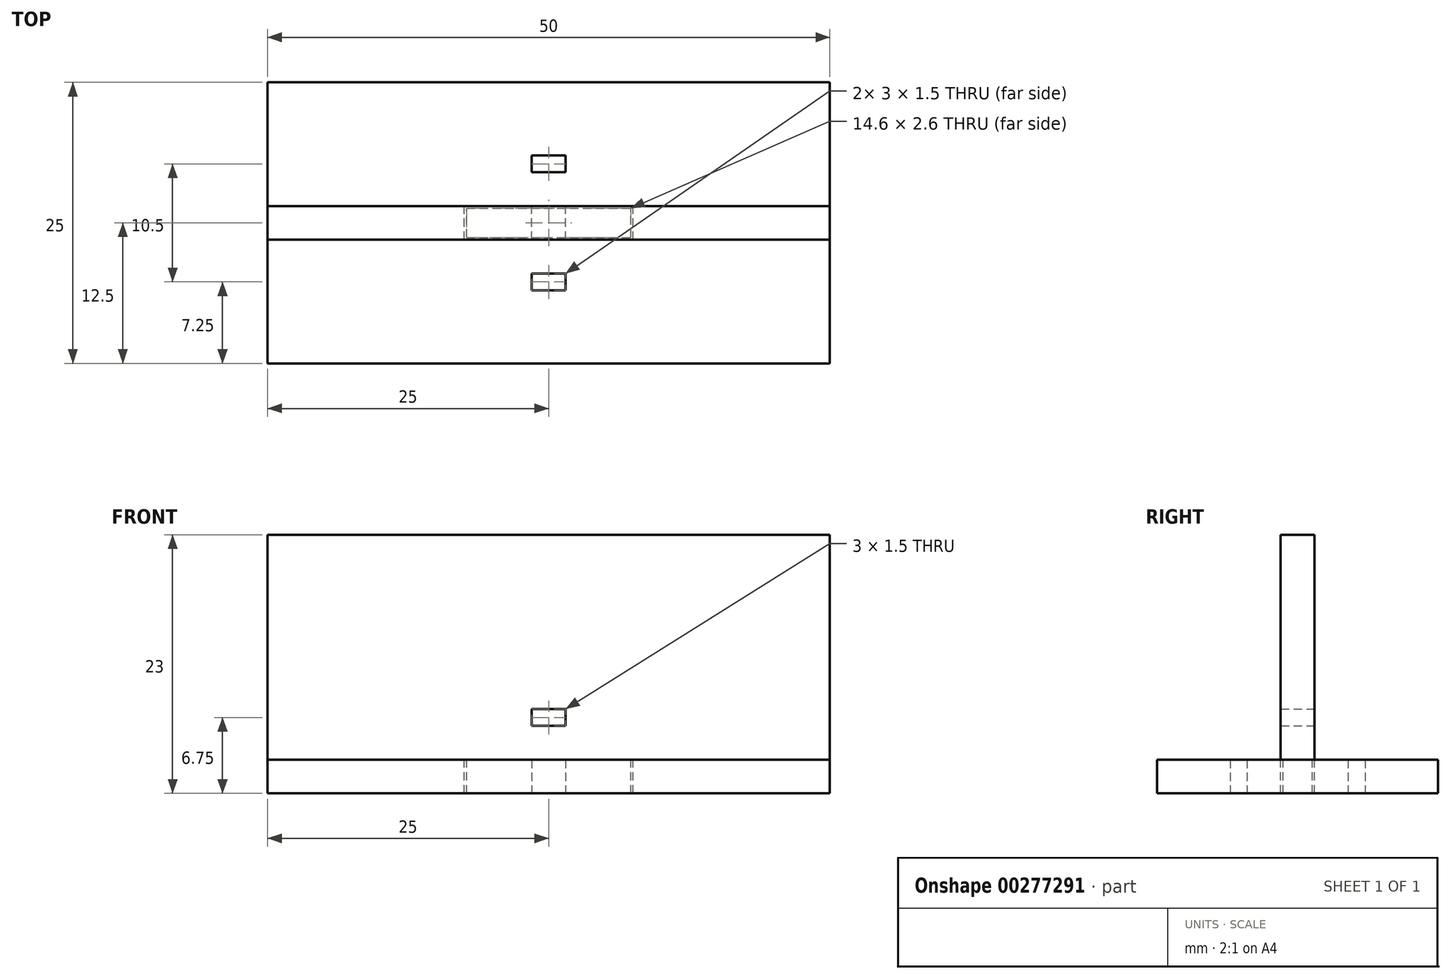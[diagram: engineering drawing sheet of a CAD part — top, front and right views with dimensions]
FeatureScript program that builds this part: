
annotation { "Feature Type Name" : "Feature", "Feature Type Description" : "" }
export const myFeature = defineFeature(function(context is Context, id is Id, definition is map)
    precondition{}
    {
        {
            assignVariable(context, id + "F0", {"name" : "StdThick", "anyValue" : 3});
        }
        {
            assignVariable(context, id + "F1", {"name" : "KerfWidth", "anyValue" : 0.2});
        }
        {
            var Q0;
            Q0=qCreatedBy(makeId("Top.planeOp"),FACE);
            var sketch = newSketch(context, id + "F2", { "sketchPlane" : qUnion([Q0])});
            skLineSegment(sketch, "E0.bottom", {"start": v(25, -12.5) * mm, "end": v(-25, -12.5) * mm});
            skLineSegment(sketch, "E0.top", {"start": v(25, 12.5) * mm, "end": v(-25, 12.5) * mm});
            skLineSegment(sketch, "E0.left", {"start": v(25, -12.5) * mm, "end": v(25, 12.5) * mm});
            skLineSegment(sketch, "E0.right", {"start": v(-25, -12.5) * mm, "end": v(-25, 12.5) * mm});
            skPoint(sketch, "E0.middle", {"position": v(0, 0) * mm});
            skSolve(sketch);
        }
        {
            var Q0;
            Q0 = qSketchRegion(id + "F2", true);
            extrude(context, id + "F3", {"entities" : qUnion([Q0]), "depth" : (getVariable(context, 'StdThick')) * mm});
        }
        {
            var Q0;
            Q0=qCreatedBy(makeId("Front.planeOp"),FACE);
            var sketch = newSketch(context, id + "F4", { "sketchPlane" : qUnion([Q0])});
            skLineSegment(sketch, "E1.0", {"start": v(25, 3) * mm, "end": v(-25, 3) * mm});
            skLineSegment(sketch, "E2", {"start": v(0, 3) * mm, "end": v(0, 0) * mm, "construction": true});
            skLineSegment(sketch, "E3", {"start": v(0, 0) * mm, "end": v(-7.5, 0) * mm});
            skLineSegment(sketch, "E4", {"start": v(-7.5, 0) * mm, "end": v(-7.5, 3) * mm});
            skLineSegment(sketch, "E5.MirrorCS", {"start": v(7.5, 0) * mm, "end": v(7.5, 3) * mm});
            skLineSegment(sketch, "E6.MirrorCS", {"start": v(0, 0) * mm, "end": v(7.5, 0) * mm});
            skLineSegment(sketch, "E7", {"start": v(-25, 3) * mm, "end": v(-25, 23) * mm});
            skLineSegment(sketch, "E8", {"start": v(-25, 23) * mm, "end": v(25, 23) * mm});
            skLineSegment(sketch, "E9", {"start": v(25, 23) * mm, "end": v(25, 3) * mm});
            skLineSegment(sketch, "E10.bottom", {"start": v(1.5, 7.5) * mm, "end": v(-1.5, 7.5) * mm});
            skLineSegment(sketch, "E10.top", {"start": v(1.5, 6) * mm, "end": v(-1.5, 6) * mm});
            skLineSegment(sketch, "E10.left", {"start": v(1.5, 7.5) * mm, "end": v(1.5, 6) * mm});
            skLineSegment(sketch, "E10.right", {"start": v(-1.5, 7.5) * mm, "end": v(-1.5, 6) * mm});
            skPoint(sketch, "E10.middle", {"position": v(0, 6.75) * mm});
            skSolve(sketch);
        }
        {
            var Q0;
            Q0 = qSketchRegion(id + "F4", true);
            extrude(context, id + "F5", {"entities" : qUnion([Q0]), "endBound" : BoundingType.SYMMETRIC, "depth" : (getVariable(context, 'StdThick')) * mm});
        }
        {
            var Q0;
            Q0=makeQuery(id+"F3.opExtrude","CAP_FACE",FACE,{"disambiguationData":[OSD([sQuery(id+"F2.wireOp",EDGE,"E0.bottom"),sQuery(id+"F2.wireOp",EDGE,"E0.top"),sQuery(id+"F2.wireOp",EDGE,"E0.left"),sQuery(id+"F2.wireOp",EDGE,"E0.right")])],"isStart":true});
            var sketch = newSketch(context, id + "F6", { "sketchPlane" : qUnion([Q0])});
            skLineSegment(sketch, "E11.0", {"start": v(-7.5, -1.5) * mm, "end": v(7.5, -1.5) * mm, "construction": true});
            skLineSegment(sketch, "E12", {"start": v(0, -1.5) * mm, "end": v(0, -5.25) * mm, "construction": true});
            skPoint(sketch, "E12.endSnap0", {"position": v(0, -1.5) * mm});
            skLineSegment(sketch, "E13.bottom", {"start": v(-1.5, -4.5) * mm, "end": v(1.5, -4.5) * mm});
            skLineSegment(sketch, "E13.top", {"start": v(-1.5, -6) * mm, "end": v(1.5, -6) * mm});
            skLineSegment(sketch, "E13.left", {"start": v(-1.5, -4.5) * mm, "end": v(-1.5, -6) * mm});
            skLineSegment(sketch, "E13.right", {"start": v(1.5, -4.5) * mm, "end": v(1.5, -6) * mm});
            skPoint(sketch, "E13.middle", {"position": v(0, -5.25) * mm});
            skLineSegment(sketch, "E14", {"start": v(0, 0) * mm, "end": v(-12.33, 0) * mm, "construction": true});
            skLineSegment(sketch, "E15.MirrorCS", {"start": v(1.5, 4.5) * mm, "end": v(1.5, 6) * mm});
            skLineSegment(sketch, "E16.MirrorCS", {"start": v(-1.5, 4.5) * mm, "end": v(1.5, 4.5) * mm});
            skLineSegment(sketch, "E17.MirrorCS", {"start": v(-1.5, 4.5) * mm, "end": v(-1.5, 6) * mm});
            skLineSegment(sketch, "E18.MirrorCS", {"start": v(-1.5, 6) * mm, "end": v(1.5, 6) * mm});
            skSolve(sketch);
        }
        {
            var Q0;
            Q0 = qSketchRegion(id + "F6", true);
            extrude(context, id + "F7", {"entities" : qUnion([Q0]), "operationType" : NewBodyOperationType.REMOVE, "oppositeDirection" : true, "depth" : 25 * mm});
        }
        {
            var Q0;
            Q0=makeQuery(id+"F5.opExtrude","SWEPT_BODY",BODY,{"disambiguationData":[OSD([sQuery(id+"F4.wireOp",EDGE,"E1.0"),sQuery(id+"F4.wireOp",EDGE,"E3"),sQuery(id+"F4.wireOp",EDGE,"E4"),sQuery(id+"F4.wireOp",EDGE,"E5.MirrorCS"),sQuery(id+"F4.wireOp",EDGE,"E6.MirrorCS"),sQuery(id+"F4.wireOp",EDGE,"E7"),sQuery(id+"F4.wireOp",EDGE,"E8"),sQuery(id+"F4.wireOp",EDGE,"E9"),sQuery(id+"F4.wireOp",EDGE,"E10.bottom"),sQuery(id+"F4.wireOp",EDGE,"E10.top"),sQuery(id+"F4.wireOp",EDGE,"E10.left"),sQuery(id+"F4.wireOp",EDGE,"E10.right")])]});
            var Q1;
            Q1=makeQuery(id+"F3.opExtrude","SWEPT_BODY",BODY,{"disambiguationData":[OSD([sQuery(id+"F2.wireOp",EDGE,"E0.bottom"),sQuery(id+"F2.wireOp",EDGE,"E0.top"),sQuery(id+"F2.wireOp",EDGE,"E0.left"),sQuery(id+"F2.wireOp",EDGE,"E0.right")])]});
            var Q2;
            Q2=makeQuery(id+"F5.opExtrude","SWEPT_FACE",FACE,{"disambiguationData":[OSD([sQuery(id+"F4.wireOp",EDGE,"E4")])]});
            var Q3;
            Q3=makeQuery(id+"F5.opExtrude","CAP_FACE",FACE,{"disambiguationData":[OSD([sQuery(id+"F4.wireOp",EDGE,"E1.0"),sQuery(id+"F4.wireOp",EDGE,"E3"),sQuery(id+"F4.wireOp",EDGE,"E4"),sQuery(id+"F4.wireOp",EDGE,"E5.MirrorCS"),sQuery(id+"F4.wireOp",EDGE,"E6.MirrorCS"),sQuery(id+"F4.wireOp",EDGE,"E7"),sQuery(id+"F4.wireOp",EDGE,"E8"),sQuery(id+"F4.wireOp",EDGE,"E9"),sQuery(id+"F4.wireOp",EDGE,"E10.bottom"),sQuery(id+"F4.wireOp",EDGE,"E10.top"),sQuery(id+"F4.wireOp",EDGE,"E10.left"),sQuery(id+"F4.wireOp",EDGE,"E10.right")])],"isStart":false});
            var Q4;
            Q4=makeQuery(id+"F5.opExtrude","SWEPT_FACE",FACE,{"disambiguationData":[OSD([sQuery(id+"F4.wireOp",EDGE,"E5.MirrorCS")])]});
            var Q5;
            Q5=makeQuery(id+"F5.opExtrude","CAP_FACE",FACE,{"disambiguationData":[OSD([sQuery(id+"F4.wireOp",EDGE,"E1.0"),sQuery(id+"F4.wireOp",EDGE,"E3"),sQuery(id+"F4.wireOp",EDGE,"E4"),sQuery(id+"F4.wireOp",EDGE,"E5.MirrorCS"),sQuery(id+"F4.wireOp",EDGE,"E6.MirrorCS"),sQuery(id+"F4.wireOp",EDGE,"E7"),sQuery(id+"F4.wireOp",EDGE,"E8"),sQuery(id+"F4.wireOp",EDGE,"E9"),sQuery(id+"F4.wireOp",EDGE,"E10.bottom"),sQuery(id+"F4.wireOp",EDGE,"E10.top"),sQuery(id+"F4.wireOp",EDGE,"E10.left"),sQuery(id+"F4.wireOp",EDGE,"E10.right")])],"isStart":true});
            booleanBodies(context, id + "F8", {"operationType" : BooleanOperationType.SUBTRACTION, "tools" : qUnion([Q0]), "targets" : qUnion([Q1]), "offset" : true, "entitiesToOffset" : qUnion([Q2, Q3, Q4, Q5]), "offsetDistance" : (getVariable(context, 'KerfWidth')) * mm, "oppositeDirection" : true, "keepTools" : true});
        }
    });
